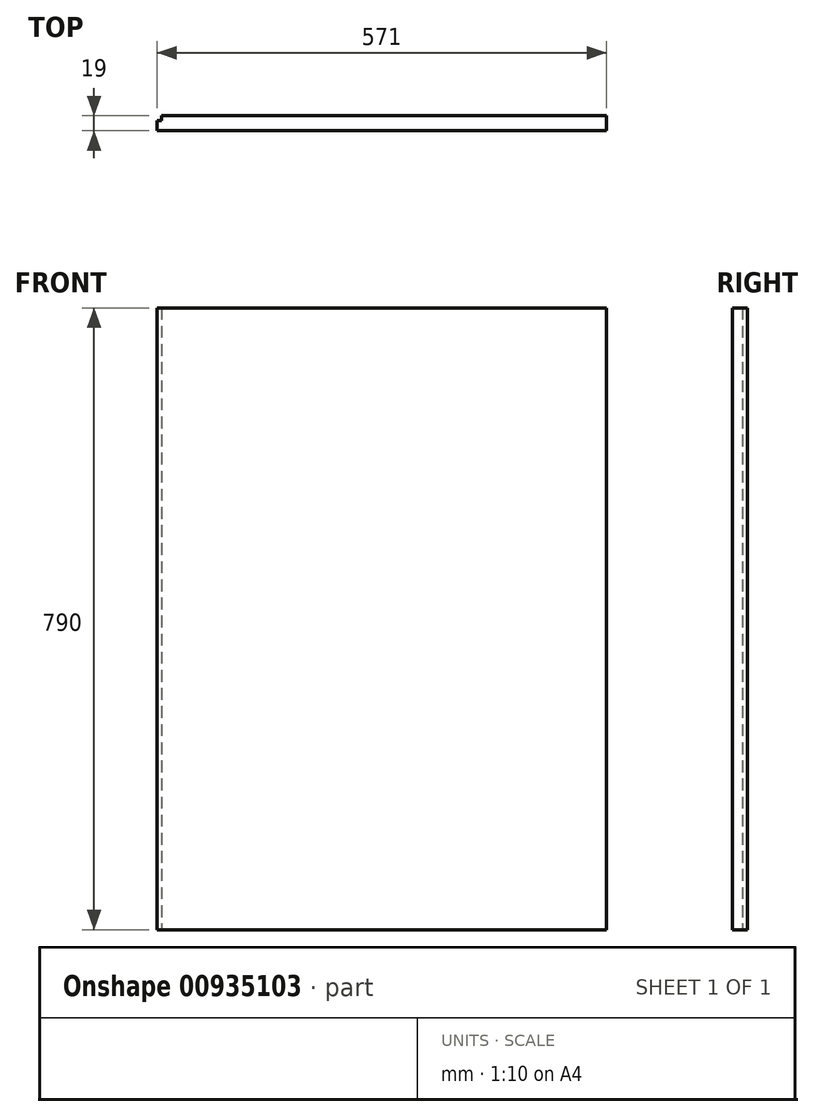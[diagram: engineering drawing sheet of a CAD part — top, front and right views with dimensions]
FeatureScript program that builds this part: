
annotation { "Feature Type Name" : "Feature", "Feature Type Description" : "" }
export const myFeature = defineFeature(function(context is Context, id is Id, definition is map)
    precondition{}
    {
        {
            var Q0;
            Q0=qCreatedBy(makeId("Front.planeOp"),FACE);
            var sketch = newSketch(context, id + "F0", { "sketchPlane" : qUnion([Q0])});
            skLineSegment(sketch, "E0.bottom", {"start": v(0, 0) * mm, "end": v(571, 0) * mm});
            skLineSegment(sketch, "E0.top", {"start": v(0, 790) * mm, "end": v(571, 790) * mm});
            skLineSegment(sketch, "E0.left", {"start": v(0, 0) * mm, "end": v(0, 790) * mm});
            skLineSegment(sketch, "E0.right", {"start": v(571, 0) * mm, "end": v(571, 790) * mm});
            skSolve(sketch);
        }
        {
            var Q0;
            Q0=makeQuery(id+"F0.imprint","IMPRINT",FACE,{"disambiguationData":[TD([[makeQuery(id+"F0.imprint","IMPRINT",EDGE,{"derivedFrom":sQuery(id+"F0.wireOp",EDGE,"E0.bottom")}),1.0]])]});
            extrude(context, id + "F1", {"entities" : qUnion([Q0]), "depth" : 19 * mm, "offsetDistance" : 25 * mm});
        }
        {
            var Q0;
            Q0=qCreatedBy(makeId("Top.planeOp"),FACE);
            var sketch = newSketch(context, id + "F2", { "sketchPlane" : qUnion([Q0])});
            skLineSegment(sketch, "E1.bottom", {"start": v(0, 0) * mm, "end": v(6, 0) * mm});
            skLineSegment(sketch, "E1.top", {"start": v(0, -6) * mm, "end": v(6, -6) * mm});
            skLineSegment(sketch, "E1.left", {"start": v(0, 0) * mm, "end": v(0, -6) * mm});
            skLineSegment(sketch, "E1.right", {"start": v(6, 0) * mm, "end": v(6, -6) * mm});
            skSolve(sketch);
        }
        {
            var Q0;
            Q0 = qSketchRegion(id + "F2", true);
            extrude(context, id + "F3", {"entities" : qUnion([Q0]), "operationType" : NewBodyOperationType.REMOVE, "endBound" : BoundingType.THROUGH_ALL, "depth" : 25 * mm, "offsetDistance" : 25 * mm});
        }
    });
